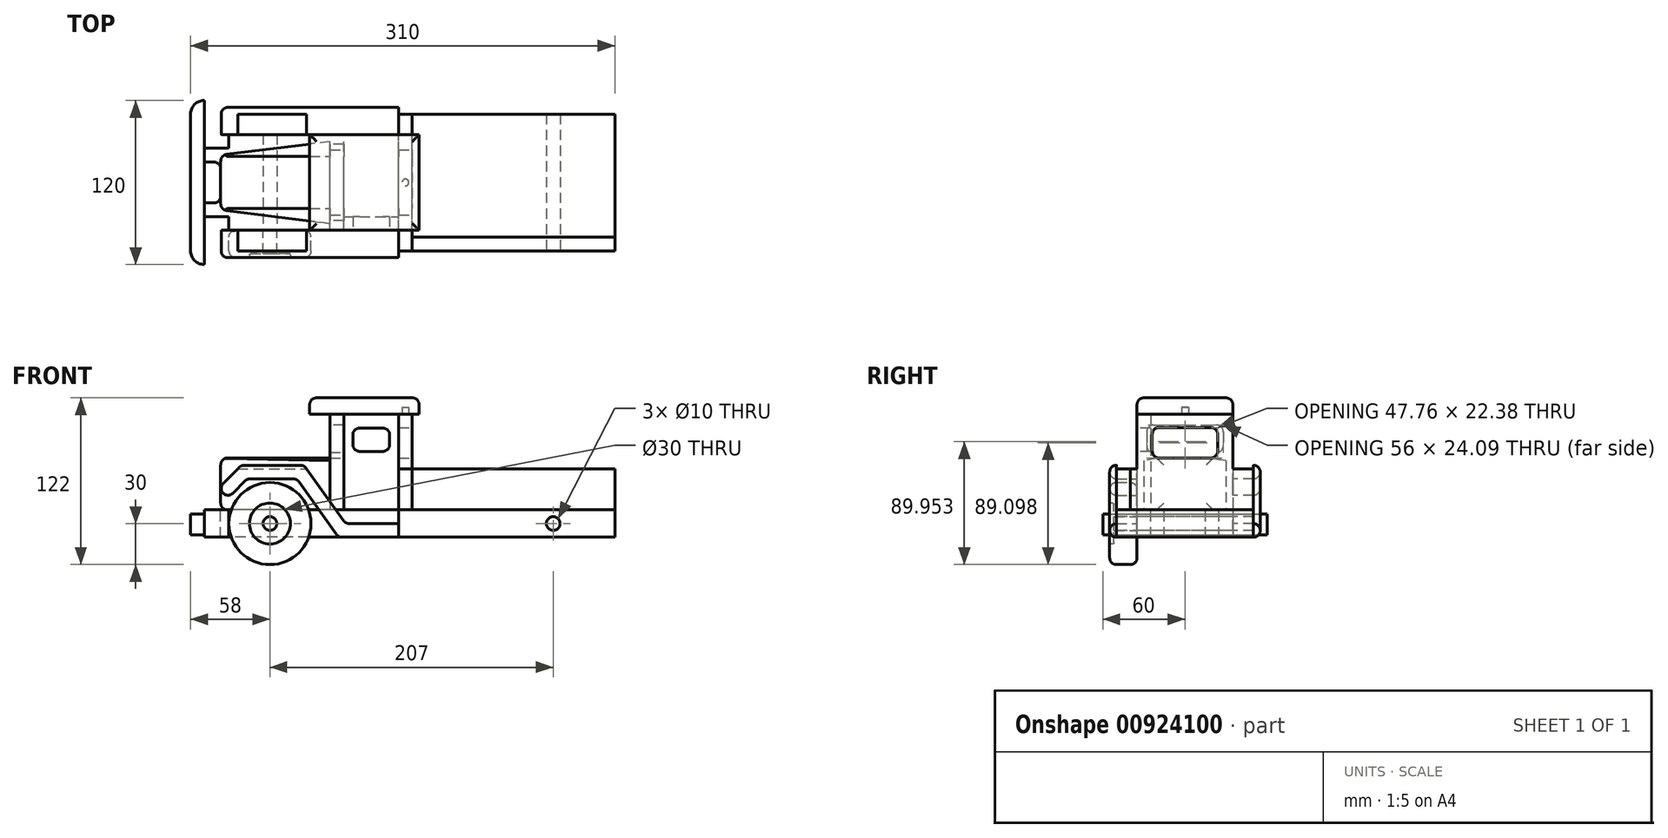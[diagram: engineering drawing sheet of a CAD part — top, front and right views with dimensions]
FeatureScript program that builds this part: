
annotation { "Feature Type Name" : "Feature", "Feature Type Description" : "" }
export const myFeature = defineFeature(function(context is Context, id is Id, definition is map)
    precondition{}
    {
        {
            var Q0;
            Q0=qCreatedBy(makeId("Top.planeOp"),FACE);
            var sketch = newSketch(context, id + "F0", { "sketchPlane" : qUnion([Q0])});
            skLineSegment(sketch, "E0.bottom", {"start": v(-8, 35) * mm, "end": v(-150, 35) * mm});
            skLineSegment(sketch, "E0.top", {"start": v(-8, -35) * mm, "end": v(-150, -35) * mm});
            skLineSegment(sketch, "E0.left", {"start": v(150, 50) * mm, "end": v(150, -50) * mm});
            skLineSegment(sketch, "E0.right", {"start": v(-150, 35) * mm, "end": v(-150, -35) * mm});
            skPoint(sketch, "E0.middle", {"position": v(0, 0) * mm});
            skLineSegment(sketch, "E1", {"start": v(-8, 35) * mm, "end": v(-8, 50) * mm});
            skLineSegment(sketch, "E2", {"start": v(-8, 50) * mm, "end": v(150, 50) * mm});
            skPoint(sketch, "E3.orphan", {"position": v(150, 35) * mm});
            skLineSegment(sketch, "E4", {"start": v(0, 0) * mm, "end": v(192.87, 0) * mm, "construction": true});
            skLineSegment(sketch, "E5.MirrorCS", {"start": v(-8, -50) * mm, "end": v(150, -50) * mm});
            skLineSegment(sketch, "E6.MirrorCS", {"start": v(-8, -35) * mm, "end": v(-8, -50) * mm});
            skPoint(sketch, "E7.MirrorP", {"position": v(150, -35) * mm});
            skSolve(sketch);
        }
        {
            var Q0;
            Q0 = qSketchRegion(id + "F0", true);
            extrude(context, id + "F1", {"entities" : qUnion([Q0]), "depth" : 20 * mm, "offsetDistance" : 25 * mm});
        }
        {
            var Q0;
            Q0=makeQuery(id+"F1.opExtrude","CAP_FACE",FACE,{"disambiguationData":[OSD([sQuery(id+"F0.wireOp",EDGE,"E0.bottom"),sQuery(id+"F0.wireOp",EDGE,"E0.top"),sQuery(id+"F0.wireOp",EDGE,"E0.left"),sQuery(id+"F0.wireOp",EDGE,"E0.right")])],"isStart":false});
            var sketch = newSketch(context, id + "F2", { "sketchPlane" : qUnion([Q0])});
            skLineSegment(sketch, "E8.bottom", {"start": v(-150, 35) * mm, "end": v(-132, 35) * mm});
            skLineSegment(sketch, "E8.top", {"start": v(-150, 25) * mm, "end": v(-132, 25) * mm});
            skLineSegment(sketch, "E8.left", {"start": v(-150, 35) * mm, "end": v(-150, 25) * mm});
            skLineSegment(sketch, "E8.right", {"start": v(-132, 35) * mm, "end": v(-132, 25) * mm});
            skLineSegment(sketch, "E9.bottom", {"start": v(-150, -35) * mm, "end": v(-132, -35) * mm});
            skLineSegment(sketch, "E9.top", {"start": v(-150, -25) * mm, "end": v(-132, -25) * mm});
            skLineSegment(sketch, "E9.left", {"start": v(-150, -35) * mm, "end": v(-150, -25) * mm});
            skLineSegment(sketch, "E9.right", {"start": v(-132, -35) * mm, "end": v(-132, -25) * mm});
            skSolve(sketch);
        }
        {
            var Q0;
            Q0 = qSketchRegion(id + "F2", true);
            extrude(context, id + "F3", {"entities" : qUnion([Q0]), "operationType" : NewBodyOperationType.REMOVE, "endBound" : BoundingType.THROUGH_ALL, "oppositeDirection" : true, "depth" : 25 * mm, "offsetDistance" : 25 * mm});
        }
        {
            var Q0;
            Q0=makeQuery(id+"F1.opExtrude","CAP_FACE",FACE,{"disambiguationData":[OSD([sQuery(id+"F0.wireOp",EDGE,"E0.bottom"),sQuery(id+"F0.wireOp",EDGE,"E0.top"),sQuery(id+"F0.wireOp",EDGE,"E0.left"),sQuery(id+"F0.wireOp",EDGE,"E0.right")])],"isStart":false});
            var sketch = newSketch(context, id + "F4", { "sketchPlane" : qUnion([Q0])});
            skLineSegment(sketch, "E10.bottom", {"start": v(-150, 15) * mm, "end": v(-143, 15) * mm});
            skLineSegment(sketch, "E10.top", {"start": v(-150, -15) * mm, "end": v(-143, -15) * mm});
            skLineSegment(sketch, "E10.left", {"start": v(-150, 15) * mm, "end": v(-150, -15) * mm});
            skLineSegment(sketch, "E10.right", {"start": v(-138, 10) * mm, "end": v(-138, -10) * mm});
            skPoint(sketch, "E11.visualSharp", {"position": v(-138, 15) * mm});
            skArc(sketch, "E11.filletArc", {"start": v(-138, 10) * mm, "mid": v(-139.46, 13.54) * mm, "end": v(-143, 15) * mm});
            skPoint(sketch, "E12.visualSharp", {"position": v(-138, -15) * mm});
            skArc(sketch, "E12.filletArc", {"start": v(-143, -15) * mm, "mid": v(-139.46, -13.54) * mm, "end": v(-138, -10) * mm});
            skSolve(sketch);
        }
        {
            var Q0;
            Q0 = qSketchRegion(id + "F4", true);
            extrude(context, id + "F5", {"entities" : qUnion([Q0]), "operationType" : NewBodyOperationType.REMOVE, "endBound" : BoundingType.THROUGH_ALL, "oppositeDirection" : true, "depth" : 25 * mm, "offsetDistance" : 25 * mm});
        }
        {
            var Q0;
            Q0=makeQuery(id+"F1.opExtrude","CAP_FACE",FACE,{"disambiguationData":[OSD([sQuery(id+"F0.wireOp",EDGE,"E0.bottom"),sQuery(id+"F0.wireOp",EDGE,"E0.top"),sQuery(id+"F0.wireOp",EDGE,"E0.left"),sQuery(id+"F0.wireOp",EDGE,"E0.right")])],"isStart":false});
            var sketch = newSketch(context, id + "F6", { "sketchPlane" : qUnion([Q0])});
            skLineSegment(sketch, "E13.bottom", {"start": v(-58, -35) * mm, "end": v(-48, -35) * mm});
            skLineSegment(sketch, "E13.top", {"start": v(-58, 35) * mm, "end": v(-48, 35) * mm});
            skLineSegment(sketch, "E13.left", {"start": v(-58, -35) * mm, "end": v(-58, 35) * mm});
            skLineSegment(sketch, "E13.right", {"start": v(-48, -35) * mm, "end": v(-48, 35) * mm});
            skSolve(sketch);
        }
        {
            var Q0;
            Q0 = qSketchRegion(id + "F6", true);
            extrude(context, id + "F7", {"entities" : qUnion([Q0]), "depth" : 70 * mm, "offsetDistance" : 25 * mm});
        }
        {
            var Q0;
            Q0=makeQuery(id+"F7.opExtrude","SWEPT_FACE",FACE,{"disambiguationData":[OSD([sQuery(id+"F6.wireOp",EDGE,"E13.left")])]});
            var sketch = newSketch(context, id + "F8", { "sketchPlane" : qUnion([Q0])});
            skLineSegment(sketch, "E14", {"start": v(0, 61.29) * mm, "end": v(30, 56) * mm});
            skLineSegment(sketch, "E15", {"start": v(30, 56) * mm, "end": v(30, 20) * mm});
            skLineSegment(sketch, "E16", {"start": v(30, 20) * mm, "end": v(0, 20) * mm});
            skLineSegment(sketch, "E17", {"start": v(0, 20) * mm, "end": v(0, 68.79) * mm, "construction": true});
            skLineSegment(sketch, "E18.MirrorCS", {"start": v(0, 61.29) * mm, "end": v(-30, 56) * mm});
            skLineSegment(sketch, "E19.MirrorCS", {"start": v(-30, 56) * mm, "end": v(-30, 20) * mm});
            skLineSegment(sketch, "E20.MirrorCS", {"start": v(-30, 20) * mm, "end": v(0, 20) * mm});
            skSolve(sketch);
        }
        {
            var Q0;
            Q0 = qSketchRegion(id + "F8", true);
            extrude(context, id + "F9", {"entities" : qUnion([Q0]), "depth" : 80 * mm, "offsetDistance" : 25 * mm});
        }
        {
            var Q0;
            Q0=makeQuery(id+"F9.opExtrude","SWEPT_FACE",FACE,{"disambiguationData":[OSD([sQuery(id+"F8.wireOp",EDGE,"E16"),sQuery(id+"F8.wireOp",EDGE,"E20.MirrorCS")])]});
            var sketch = newSketch(context, id + "F10", { "sketchPlane" : qUnion([Q0])});
            skLineSegment(sketch, "E21", {"start": v(-58, 30) * mm, "end": v(-138, 20) * mm});
            skLineSegment(sketch, "E22.0", {"start": v(-138, 30) * mm, "end": v(-138, 20) * mm});
            skLineSegment(sketch, "E22.1", {"start": v(-138, 30) * mm, "end": v(-58, 30) * mm});
            skPoint(sketch, "E23.orphan", {"position": v(-138, -30) * mm});
            skLineSegment(sketch, "E24", {"start": v(-58, 0) * mm, "end": v(-100.02, 0) * mm, "construction": true});
            skLineSegment(sketch, "E25.MirrorCS", {"start": v(-58, -30) * mm, "end": v(-138, -20) * mm});
            skLineSegment(sketch, "E26.MirrorCS", {"start": v(-138, -30) * mm, "end": v(-138, -20) * mm});
            skLineSegment(sketch, "E27.MirrorCS", {"start": v(-138, -30) * mm, "end": v(-58, -30) * mm});
            skPoint(sketch, "E28.MirrorP", {"position": v(-138, 30) * mm});
            skSolve(sketch);
        }
        {
            var Q0;
            Q0 = qSketchRegion(id + "F10", true);
            extrude(context, id + "F11", {"entities" : qUnion([Q0]), "operationType" : NewBodyOperationType.REMOVE, "endBound" : BoundingType.THROUGH_ALL, "oppositeDirection" : true, "depth" : 25 * mm, "offsetDistance" : 25 * mm});
        }
        {
            var Q0;
            Q0=makeQuery(id+"F7.opExtrude","SWEPT_FACE",FACE,{"disambiguationData":[OSD([sQuery(id+"F6.wireOp",EDGE,"E13.left")])]});
            var sketch = newSketch(context, id + "F12", { "sketchPlane" : qUnion([Q0])});
            skLineSegment(sketch, "E29.bottom", {"start": v(23, 82) * mm, "end": v(-23, 82) * mm});
            skLineSegment(sketch, "E29.top", {"start": v(23, 62) * mm, "end": v(-23, 62) * mm});
            skLineSegment(sketch, "E29.left", {"start": v(28, 77) * mm, "end": v(28, 67) * mm});
            skLineSegment(sketch, "E29.right", {"start": v(-28, 77) * mm, "end": v(-28, 67) * mm});
            skPoint(sketch, "E29.middle", {"position": v(0, 72) * mm});
            skPoint(sketch, "E29.middle.positionSnap0", {"position": v(0, 90) * mm});
            skPoint(sketch, "E29.centerSnap0", {"position": v(0, 90) * mm});
            skPoint(sketch, "E30.visualSharp", {"position": v(-28, 82) * mm});
            skArc(sketch, "E30.filletArc", {"start": v(-23, 82) * mm, "mid": v(-26.54, 80.54) * mm, "end": v(-28, 77) * mm});
            skPoint(sketch, "E31.visualSharp", {"position": v(-28, 62) * mm});
            skArc(sketch, "E31.filletArc", {"start": v(-28, 67) * mm, "mid": v(-26.54, 63.46) * mm, "end": v(-23, 62) * mm});
            skPoint(sketch, "E32.visualSharp", {"position": v(28, 62) * mm});
            skArc(sketch, "E32.filletArc", {"start": v(23, 62) * mm, "mid": v(26.54, 63.46) * mm, "end": v(28, 67) * mm});
            skPoint(sketch, "E33.visualSharp", {"position": v(28, 82) * mm});
            skArc(sketch, "E33.filletArc", {"start": v(28, 77) * mm, "mid": v(26.54, 80.54) * mm, "end": v(23, 82) * mm});
            skSolve(sketch);
        }
        {
            var Q0;
            Q0 = qSketchRegion(id + "F12", true);
            extrude(context, id + "F13", {"entities" : qUnion([Q0]), "operationType" : NewBodyOperationType.REMOVE, "endBound" : BoundingType.THROUGH_ALL, "oppositeDirection" : true, "depth" : 25 * mm, "offsetDistance" : 25 * mm});
        }
        {
            var Q0;
            Q0=makeQuery(id+"F1.opExtrude","CAP_FACE",FACE,{"disambiguationData":[OSD([sQuery(id+"F0.wireOp",EDGE,"E0.bottom"),sQuery(id+"F0.wireOp",EDGE,"E0.top"),sQuery(id+"F0.wireOp",EDGE,"E0.left"),sQuery(id+"F0.wireOp",EDGE,"E0.right")])],"isStart":false});
            var sketch = newSketch(context, id + "F14", { "sketchPlane" : qUnion([Q0])});
            skLineSegment(sketch, "E34.bottom", {"start": v(-48, -35) * mm, "end": v(-8, -35) * mm});
            skLineSegment(sketch, "E34.top", {"start": v(-48, -25) * mm, "end": v(-8, -25) * mm});
            skLineSegment(sketch, "E34.left", {"start": v(-48, -35) * mm, "end": v(-48, -25) * mm});
            skLineSegment(sketch, "E34.right", {"start": v(-8, -35) * mm, "end": v(-8, -25) * mm});
            skSolve(sketch);
        }
        {
            var Q0;
            Q0 = qSketchRegion(id + "F14", true);
            extrude(context, id + "F15", {"entities" : qUnion([Q0]), "depth" : 70 * mm, "offsetDistance" : 25 * mm});
        }
        {
            var Q0;
            Q0=makeQuery(id+"F1.opExtrude","CAP_FACE",FACE,{"disambiguationData":[OSD([sQuery(id+"F0.wireOp",EDGE,"E0.bottom"),sQuery(id+"F0.wireOp",EDGE,"E0.top"),sQuery(id+"F0.wireOp",EDGE,"E0.left"),sQuery(id+"F0.wireOp",EDGE,"E0.right")])],"isStart":false});
            var sketch = newSketch(context, id + "F16", { "sketchPlane" : qUnion([Q0])});
            skLineSegment(sketch, "E35.bottom", {"start": v(-8, -50) * mm, "end": v(2, -50) * mm});
            skLineSegment(sketch, "E35.top", {"start": v(-8, 50) * mm, "end": v(2, 50) * mm});
            skLineSegment(sketch, "E35.left", {"start": v(-8, -50) * mm, "end": v(-8, 50) * mm});
            skLineSegment(sketch, "E35.right", {"start": v(2, -50) * mm, "end": v(2, 50) * mm});
            skSolve(sketch);
        }
        {
            var Q0;
            Q0 = qSketchRegion(id + "F16", true);
            extrude(context, id + "F17", {"entities" : qUnion([Q0]), "depth" : 70 * mm, "offsetDistance" : 25 * mm});
        }
        {
            var Q0;
            Q0=makeQuery(id+"F17.opExtrude","CAP_FACE",FACE,{"disambiguationData":[OSD([sQuery(id+"F16.wireOp",EDGE,"E35.bottom"),sQuery(id+"F16.wireOp",EDGE,"E35.top"),sQuery(id+"F16.wireOp",EDGE,"E35.left"),sQuery(id+"F16.wireOp",EDGE,"E35.right")])],"isStart":false});
            var sketch = newSketch(context, id + "F18", { "sketchPlane" : qUnion([Q0])});
            skLineSegment(sketch, "E36.bottom", {"start": v(7, 35) * mm, "end": v(-73, 35) * mm});
            skLineSegment(sketch, "E36.top", {"start": v(7, -35) * mm, "end": v(-73, -35) * mm});
            skLineSegment(sketch, "E36.left", {"start": v(7, 35) * mm, "end": v(7, -35) * mm});
            skLineSegment(sketch, "E36.right", {"start": v(-73, 35) * mm, "end": v(-73, -35) * mm});
            skPoint(sketch, "E36.middle", {"position": v(-174.54, 0) * mm});
            skPoint(sketch, "E36.middle.positionSnap0", {"position": v(2, 0) * mm});
            skPoint(sketch, "E36.centerSnap0", {"position": v(2, 0) * mm});
            skSolve(sketch);
        }
        {
            var Q0;
            Q0 = qSketchRegion(id + "F18", true);
            extrude(context, id + "F19", {"entities" : qUnion([Q0]), "depth" : 12 * mm, "offsetDistance" : 25 * mm});
        }
        {
            var Q0;
            Q0=makeQuery(id+"F1.opExtrude","CAP_FACE",FACE,{"disambiguationData":[OSD([sQuery(id+"F0.wireOp",EDGE,"E0.bottom"),sQuery(id+"F0.wireOp",EDGE,"E0.top"),sQuery(id+"F0.wireOp",EDGE,"E0.left"),sQuery(id+"F0.wireOp",EDGE,"E0.right")])],"isStart":false});
            var sketch = newSketch(context, id + "F20", { "sketchPlane" : qUnion([Q0])});
            skLineSegment(sketch, "E37.bottom", {"start": v(2, -50) * mm, "end": v(150, -50) * mm});
            skLineSegment(sketch, "E37.top", {"start": v(2, -40) * mm, "end": v(150, -40) * mm});
            skLineSegment(sketch, "E37.left", {"start": v(2, -50) * mm, "end": v(2, -40) * mm});
            skLineSegment(sketch, "E37.right", {"start": v(150, -50) * mm, "end": v(150, -40) * mm});
            skSolve(sketch);
        }
        {
            var Q0;
            Q0 = qSketchRegion(id + "F20", true);
            extrude(context, id + "F21", {"entities" : qUnion([Q0]), "depth" : 30 * mm, "offsetDistance" : 25 * mm});
        }
        {
            var Q0;
            Q0=makeQuery(id+"F1.opExtrude","SWEPT_FACE",FACE,{"disambiguationData":[OSD([sQuery(id+"F0.wireOp",EDGE,"E0.top")])]});
            var sketch = newSketch(context, id + "F22", { "sketchPlane" : qUnion([Q0])});
            skCircle(sketch, "E38", {"center": v(-102, 10) * mm, "radius": 5 * mm});
            skPoint(sketch, "E38.centerSnap0", {"position": v(-132, 10) * mm});
            skCircle(sketch, "E39", {"center": v(105, 10) * mm, "radius": 5 * mm});
            skPoint(sketch, "E39.centerSnap0", {"position": v(150, 10) * mm});
            skSolve(sketch);
        }
        {
            var Q0;
            Q0 = qSketchRegion(id + "F22", true);
            extrude(context, id + "F23", {"entities" : qUnion([Q0]), "operationType" : NewBodyOperationType.REMOVE, "endBound" : BoundingType.THROUGH_ALL, "oppositeDirection" : true, "depth" : 25 * mm, "offsetDistance" : 25 * mm, "hasSecondDirection" : true, "secondDirectionBound" : SecondDirectionBoundingType.THROUGH_ALL, "secondDirectionOppositeDirection" : false, "secondDirectionDepth" : 25 * mm});
        }
        {
            var Q0;
            Q0=makeQuery(id+"F1.opExtrude","SWEPT_FACE",FACE,{"disambiguationData":[OSD([sQuery(id+"F0.wireOp",EDGE,"E0.top")])]});
            var sketch = newSketch(context, id + "F24", { "sketchPlane" : qUnion([Q0])});
            skCircle(sketch, "E40", {"center": v(-102, 10) * mm, "radius": 30 * mm});
            skCircle(sketch, "E41", {"center": v(-102, 10) * mm, "radius": 5 * mm});
            skSolve(sketch);
        }
        {
            var Q0;
            Q0 = qSketchRegion(id + "F24", true);
            extrude(context, id + "F25", {"entities" : qUnion([Q0]), "depth" : 20 * mm, "offsetDistance" : 25 * mm});
        }
        {
            var Q0;
            Q0=makeQuery(id+"F25.opExtrude","CAP_EDGE",EDGE,{"disambiguationData":[OSD([sQuery(id+"F24.wireOp",EDGE,"E40")])],"isStart":false});
            var Q1;
            Q1=makeQuery(id+"F25.opExtrude","CAP_EDGE",EDGE,{"disambiguationData":[OSD([sQuery(id+"F24.wireOp",EDGE,"E40")])],"isStart":true});
            fillet(context, id + "F26", {"entities" : qUnion([Q0, Q1]), "radius" : 5 * mm, "tangentPropagation" : true, "allowEdgeOverflow" : false});
        }
        {
            var Q0;
            Q0=makeQuery(id+"F25.opExtrude","CAP_FACE",FACE,{"disambiguationData":[OSD([sQuery(id+"F24.wireOp",EDGE,"E40"),sQuery(id+"F24.wireOp",EDGE,"E41")])],"isStart":false});
            var sketch = newSketch(context, id + "F27", { "sketchPlane" : qUnion([Q0])});
            skCircle(sketch, "E42", {"center": v(-102, 10) * mm, "radius": 15 * mm});
            skSolve(sketch);
        }
        {
            var Q0;
            Q0 = qSketchRegion(id + "F27", true);
            extrude(context, id + "F28", {"entities" : qUnion([Q0]), "operationType" : NewBodyOperationType.REMOVE, "oppositeDirection" : true, "depth" : 3 * mm, "offsetDistance" : 25 * mm});
        }
        {
            var Q0;
            Q0=makeQuery(id+"F28.boolean.opBoolean","COPY",EDGE,{"derivedFrom":makeQuery(id+"F28.opExtrude","CAP_EDGE",EDGE,{"disambiguationData":[OSD([sQuery(id+"F27.wireOp",EDGE,"E42")])],"isStart":false})});
            var Q1;
            Q1=makeQuery(id+"F28.boolean.opBoolean","COPY",EDGE,{"derivedFrom":makeQuery(id+"F28.opExtrude","CAP_EDGE",EDGE,{"disambiguationData":[OSD([sQuery(id+"F27.wireOp",EDGE,"E42")])],"isStart":true})});
            fillet(context, id + "F29", {"entities" : qUnion([Q0, Q1]), "radius" : 1 * mm, "tangentPropagation" : true, "allowEdgeOverflow" : false});
        }
        {
            var Q0;
            Q0=makeQuery(id+"F19.opExtrude","CAP_FACE",FACE,{"disambiguationData":[OSD([sQuery(id+"F18.wireOp",EDGE,"E36.bottom"),sQuery(id+"F18.wireOp",EDGE,"E36.top"),sQuery(id+"F18.wireOp",EDGE,"E36.left"),sQuery(id+"F18.wireOp",EDGE,"E36.right")])],"isStart":false});
            fillet(context, id + "F30", {"entities" : qUnion([Q0]), "radius" : 5 * mm, "tangentPropagation" : true, "allowEdgeOverflow" : false});
        }
        {
            var Q0;
            Q0=makeQuery(id+"F15.opExtrude","SWEPT_FACE",FACE,{"disambiguationData":[OSD([sQuery(id+"F14.wireOp",EDGE,"E34.bottom")])]});
            var sketch = newSketch(context, id + "F31", { "sketchPlane" : qUnion([Q0])});
            skLineSegment(sketch, "E43.bottom", {"start": v(-19.57, 79.88) * mm, "end": v(-36.43, 79.88) * mm});
            skLineSegment(sketch, "E43.top", {"start": v(-19.57, 62.78) * mm, "end": v(-36.43, 62.78) * mm});
            skLineSegment(sketch, "E43.left", {"start": v(-14.57, 74.88) * mm, "end": v(-14.57, 67.78) * mm});
            skLineSegment(sketch, "E43.right", {"start": v(-41.43, 74.88) * mm, "end": v(-41.43, 67.78) * mm});
            skPoint(sketch, "E43.middle", {"position": v(-28, 71.33) * mm});
            skPoint(sketch, "E43.middle.positionSnap0", {"position": v(-28, 90) * mm});
            skPoint(sketch, "E43.centerSnap0", {"position": v(-28, 90) * mm});
            skPoint(sketch, "E44.visualSharp", {"position": v(-41.43, 79.88) * mm});
            skArc(sketch, "E44.filletArc", {"start": v(-36.43, 79.88) * mm, "mid": v(-39.97, 78.42) * mm, "end": v(-41.43, 74.88) * mm});
            skPoint(sketch, "E45.visualSharp", {"position": v(-41.43, 62.78) * mm});
            skArc(sketch, "E45.filletArc", {"start": v(-41.43, 67.78) * mm, "mid": v(-39.97, 64.25) * mm, "end": v(-36.43, 62.78) * mm});
            skPoint(sketch, "E46.visualSharp", {"position": v(-14.57, 62.78) * mm});
            skArc(sketch, "E46.filletArc", {"start": v(-19.57, 62.78) * mm, "mid": v(-16.03, 64.25) * mm, "end": v(-14.57, 67.78) * mm});
            skPoint(sketch, "E47.visualSharp", {"position": v(-14.57, 79.88) * mm});
            skArc(sketch, "E47.filletArc", {"start": v(-14.57, 74.88) * mm, "mid": v(-16.03, 78.42) * mm, "end": v(-19.57, 79.88) * mm});
            skSolve(sketch);
        }
        {
            var Q0;
            Q0 = qSketchRegion(id + "F31", true);
            extrude(context, id + "F32", {"entities" : qUnion([Q0]), "operationType" : NewBodyOperationType.REMOVE, "endBound" : BoundingType.THROUGH_ALL, "oppositeDirection" : true, "depth" : 25 * mm, "offsetDistance" : 25 * mm});
        }
        {
            var Q0;
            Q0=makeQuery(id+"F19.opExtrude","CAP_FACE",FACE,{"disambiguationData":[OSD([sQuery(id+"F18.wireOp",EDGE,"E36.bottom"),sQuery(id+"F18.wireOp",EDGE,"E36.top"),sQuery(id+"F18.wireOp",EDGE,"E36.left"),sQuery(id+"F18.wireOp",EDGE,"E36.right")])],"isStart":true});
            var sketch = newSketch(context, id + "F33", { "sketchPlane" : qUnion([Q0])});
            skCircle(sketch, "E48", {"center": v(-3, 0) * mm, "radius": 2.47 * mm});
            skPoint(sketch, "E49", {"position": v(7, 0) * mm});
            skSolve(sketch);
        }
        {
            var Q0;
            Q0 = qSketchRegion(id + "F33", true);
            extrude(context, id + "F34", {"entities" : qUnion([Q0]), "operationType" : NewBodyOperationType.REMOVE, "oppositeDirection" : true, "depth" : 5 * mm, "offsetDistance" : 25 * mm});
        }
        {
            var Q0;
            Q0=makeQuery(id+"F17.opExtrude","SWEPT_FACE",FACE,{"disambiguationData":[OSD([sQuery(id+"F16.wireOp",EDGE,"E35.right")])]});
            var sketch = newSketch(context, id + "F35", { "sketchPlane" : qUnion([Q0])});
            skLineSegment(sketch, "E50.bottom", {"start": v(18.88, 80.29) * mm, "end": v(-18.88, 80.29) * mm});
            skLineSegment(sketch, "E50.top", {"start": v(18.88, 57.9) * mm, "end": v(-18.88, 57.9) * mm});
            skLineSegment(sketch, "E50.left", {"start": v(23.88, 75.29) * mm, "end": v(23.88, 62.9) * mm});
            skLineSegment(sketch, "E50.right", {"start": v(-23.88, 75.29) * mm, "end": v(-23.88, 62.9) * mm});
            skPoint(sketch, "E50.middle", {"position": v(0, 69.1) * mm});
            skPoint(sketch, "E51.visualSharp", {"position": v(-23.88, 80.29) * mm});
            skArc(sketch, "E51.filletArc", {"start": v(-18.88, 80.29) * mm, "mid": v(-22.42, 78.82) * mm, "end": v(-23.88, 75.29) * mm});
            skPoint(sketch, "E52.visualSharp", {"position": v(-23.88, 57.9) * mm});
            skArc(sketch, "E52.filletArc", {"start": v(-23.88, 62.9) * mm, "mid": v(-22.42, 59.37) * mm, "end": v(-18.88, 57.9) * mm});
            skPoint(sketch, "E53.visualSharp", {"position": v(23.88, 57.9) * mm});
            skArc(sketch, "E53.filletArc", {"start": v(18.88, 57.9) * mm, "mid": v(22.42, 59.37) * mm, "end": v(23.88, 62.9) * mm});
            skPoint(sketch, "E54.visualSharp", {"position": v(23.88, 80.29) * mm});
            skArc(sketch, "E54.filletArc", {"start": v(23.88, 75.29) * mm, "mid": v(22.42, 78.82) * mm, "end": v(18.88, 80.29) * mm});
            skSolve(sketch);
        }
        {
            var Q0;
            Q0 = qSketchRegion(id + "F35", true);
            extrude(context, id + "F36", {"entities" : qUnion([Q0]), "operationType" : NewBodyOperationType.REMOVE, "endBound" : BoundingType.THROUGH_ALL, "oppositeDirection" : true, "depth" : 25 * mm, "offsetDistance" : 25 * mm});
        }
        {
            var Q0;
            {var subQ4=sQuery(id+"F0.wireOp",EDGE,"E0.right");Q0=makeQuery(id+"F5.boolean.opBoolean","SPLIT",FACE,{"disambiguationData":[TD([makeQuery(id+"F3.boolean.opBoolean","COPY",FACE,{"derivedFrom":makeQuery(id+"F3.opExtrude","SWEPT_FACE",FACE,{"disambiguationData":[OSD([sQuery(id+"F2.wireOp",EDGE,"E8.top")])]})})])],"derivedFrom":makeQuery(id+"F1.opExtrude","SWEPT_FACE",FACE,{"disambiguationData":[OSD([subQ4])]})});}
            var sketch = newSketch(context, id + "F37", { "sketchPlane" : qUnion([Q0])});
            skLineSegment(sketch, "E55.bottom", {"start": v(60, 17.03) * mm, "end": v(-60, 17.03) * mm});
            skLineSegment(sketch, "E55.top", {"start": v(60, 1.66) * mm, "end": v(-60, 1.66) * mm});
            skLineSegment(sketch, "E55.left", {"start": v(60, 17.03) * mm, "end": v(60, 1.66) * mm});
            skLineSegment(sketch, "E55.right", {"start": v(-60, 17.03) * mm, "end": v(-60, 1.66) * mm});
            skPoint(sketch, "E55.middle", {"position": v(0, 9.35) * mm});
            skSolve(sketch);
        }
        {
            var Q0;
            Q0 = qSketchRegion(id + "F37", true);
            extrude(context, id + "F38", {"entities" : qUnion([Q0]), "depth" : 10 * mm, "offsetDistance" : 25 * mm});
        }
        {
            var Q0;
            Q0=makeQuery(id+"F38.opExtrude","CAP_EDGE",EDGE,{"disambiguationData":[OSD([sQuery(id+"F37.wireOp",EDGE,"E55.right")])],"isStart":false});
            var Q1;
            Q1=makeQuery(id+"F38.opExtrude","CAP_EDGE",EDGE,{"disambiguationData":[OSD([sQuery(id+"F37.wireOp",EDGE,"E55.left")])],"isStart":false});
            fillet(context, id + "F39", {"entities" : qUnion([Q0, Q1]), "radius" : 10 * mm, "tangentPropagation" : true, "allowEdgeOverflow" : false});
        }
        {
            var Q0;
            Q0=makeQuery(id+"F9.opExtrude","CAP_FACE",FACE,{"disambiguationData":[OSD([sQuery(id+"F8.wireOp",EDGE,"E14"),sQuery(id+"F8.wireOp",EDGE,"E15"),sQuery(id+"F8.wireOp",EDGE,"E16"),sQuery(id+"F8.wireOp",EDGE,"E18.MirrorCS"),sQuery(id+"F8.wireOp",EDGE,"E19.MirrorCS"),sQuery(id+"F8.wireOp",EDGE,"E20.MirrorCS")])],"isStart":false});
            fillet(context, id + "F40", {"entities" : qUnion([Q0]), "radius" : 5 * mm, "tangentPropagation" : true, "allowEdgeOverflow" : false});
        }
        {
            var Q0;
            Q0=makeQuery(id+"F1.opExtrude","SWEPT_FACE",FACE,{"disambiguationData":[OSD([sQuery(id+"F0.wireOp",EDGE,"E0.top")])]});
            var sketch = newSketch(context, id + "F41", { "sketchPlane" : qUnion([Q0])});
            skLineSegment(sketch, "E56", {"start": v(-129.04, 32.22) * mm, "end": v(-120.27, 41.17) * mm});
            skLineSegment(sketch, "E57", {"start": v(-116.7, 42.66) * mm, "end": v(-84.8, 42.66) * mm});
            skLineSegment(sketch, "E58", {"start": v(-80.73, 40.56) * mm, "end": v(-53.42, 2.1) * mm});
            skLineSegment(sketch, "E59.0", {"start": v(-75.56, 50.56) * mm, "end": v(-48.25, 12.1) * mm});
            skLineSegment(sketch, "E59.1", {"start": v(-120.9, 52.66) * mm, "end": v(-79.64, 52.66) * mm});
            skLineSegment(sketch, "E59.2", {"start": v(-136.18, 39.23) * mm, "end": v(-124.47, 51.17) * mm});
            skLineSegment(sketch, "E60", {"start": v(-136.11, 32.15) * mm, "end": v(-136.11, 32.15) * mm});
            skLineSegment(sketch, "E61.0", {"start": v(-8, 0) * mm, "end": v(-49.34, 0) * mm});
            skLineSegment(sketch, "E62.0", {"start": v(-8, 10) * mm, "end": v(-44.18, 10) * mm});
            skPoint(sketch, "E63.orphan", {"position": v(-132, 0) * mm});
            skLineSegment(sketch, "E64.0", {"start": v(-8, 10) * mm, "end": v(-8, 0) * mm});
            skPoint(sketch, "E65.orphan", {"position": v(-8, 20) * mm});
            skPoint(sketch, "E66.visualSharp", {"position": v(-132.54, 28.65) * mm});
            skArc(sketch, "E66.filletArc", {"start": v(-136.11, 32.15) * mm, "mid": v(-132.56, 30.72) * mm, "end": v(-129.04, 32.22) * mm});
            skPoint(sketch, "E67.visualSharp", {"position": v(-139.68, 35.66) * mm});
            skArc(sketch, "E67.filletArc", {"start": v(-136.18, 39.23) * mm, "mid": v(-137.6, 35.68) * mm, "end": v(-136.11, 32.15) * mm});
            skPoint(sketch, "E68.visualSharp", {"position": v(-123, 52.66) * mm});
            skArc(sketch, "E68.filletArc", {"start": v(-120.9, 52.66) * mm, "mid": v(-122.83, 52.27) * mm, "end": v(-124.47, 51.17) * mm});
            skPoint(sketch, "E69.visualSharp", {"position": v(-118.8, 42.66) * mm});
            skArc(sketch, "E69.filletArc", {"start": v(-116.7, 42.66) * mm, "mid": v(-118.64, 42.27) * mm, "end": v(-120.27, 41.17) * mm});
            skPoint(sketch, "E70.visualSharp", {"position": v(-82.22, 42.66) * mm});
            skArc(sketch, "E70.filletArc", {"start": v(-80.73, 40.56) * mm, "mid": v(-82.5, 42.1) * mm, "end": v(-84.8, 42.66) * mm});
            skPoint(sketch, "E71.visualSharp", {"position": v(-77.06, 52.66) * mm});
            skArc(sketch, "E71.filletArc", {"start": v(-75.56, 50.56) * mm, "mid": v(-77.35, 52.1) * mm, "end": v(-79.64, 52.66) * mm});
            skPoint(sketch, "E72.visualSharp", {"position": v(-46.76, 10) * mm});
            skArc(sketch, "E72.filletArc", {"start": v(-48.25, 12.1) * mm, "mid": v(-46.47, 10.56) * mm, "end": v(-44.18, 10) * mm});
            skPoint(sketch, "E73.visualSharp", {"position": v(-51.92, 0) * mm});
            skArc(sketch, "E73.filletArc", {"start": v(-53.42, 2.1) * mm, "mid": v(-51.63, 0.56) * mm, "end": v(-49.34, 0) * mm});
            skSolve(sketch);
        }
        {
            var Q0;
            Q0 = qSketchRegion(id + "F41", true);
            extrude(context, id + "F42", {"entities" : qUnion([Q0]), "depth" : 20 * mm, "offsetDistance" : 25 * mm});
        }
        {
            var Q0;
            Q0=makeQuery(id+"F42.opExtrude","CAP_EDGE",EDGE,{"disambiguationData":[OSD([sQuery(id+"F41.wireOp",EDGE,"E59.2")])],"isStart":false});
            fillet(context, id + "F43", {"entities" : qUnion([Q0]), "radius" : 5 * mm, "tangentPropagation" : true, "allowEdgeOverflow" : false});
        }
        {
            var Q0;
            Q0=makeQuery(id+"F42.opExtrude","SWEPT_BODY",BODY,{"disambiguationData":[OSD([sQuery(id+"F41.wireOp",EDGE,"E56"),sQuery(id+"F41.wireOp",EDGE,"E57"),sQuery(id+"F41.wireOp",EDGE,"E58"),sQuery(id+"F41.wireOp",EDGE,"E59.0"),sQuery(id+"F41.wireOp",EDGE,"E59.1"),sQuery(id+"F41.wireOp",EDGE,"E59.2"),sQuery(id+"F41.wireOp",EDGE,"E61.0"),sQuery(id+"F41.wireOp",EDGE,"E62.0"),sQuery(id+"F41.wireOp",EDGE,"E64.0"),sQuery(id+"F41.wireOp",EDGE,"E66.filletArc"),sQuery(id+"F41.wireOp",EDGE,"E67.filletArc"),sQuery(id+"F41.wireOp",EDGE,"E68.filletArc"),sQuery(id+"F41.wireOp",EDGE,"E69.filletArc"),sQuery(id+"F41.wireOp",EDGE,"E70.filletArc"),sQuery(id+"F41.wireOp",EDGE,"E71.filletArc"),sQuery(id+"F41.wireOp",EDGE,"E72.filletArc"),sQuery(id+"F41.wireOp",EDGE,"E73.filletArc")])]});
            var Q1;
            Q1=qCreatedBy(makeId("Front.planeOp"),FACE);
            mirror(context, id + "F44", {"entities" : qUnion([Q0]), "mirrorPlane" : qUnion([Q1])});
        }
        {
            var Q0;
            Q0=makeQuery(id+"F17.opExtrude","SWEPT_FACE",FACE,{"disambiguationData":[OSD([sQuery(id+"F16.wireOp",EDGE,"E35.right")])]});
            var sketch = newSketch(context, id + "F45", { "sketchPlane" : qUnion([Q0])});
            skLineSegment(sketch, "E74.bottom", {"start": v(-50, 50) * mm, "end": v(-35, 50) * mm});
            skLineSegment(sketch, "E74.top", {"start": v(-50, 90) * mm, "end": v(-35, 90) * mm});
            skLineSegment(sketch, "E74.left", {"start": v(-50, 50) * mm, "end": v(-50, 90) * mm});
            skLineSegment(sketch, "E74.right", {"start": v(-35, 50) * mm, "end": v(-35, 90) * mm});
            skLineSegment(sketch, "E75.bottom", {"start": v(50, 90) * mm, "end": v(35, 90) * mm});
            skLineSegment(sketch, "E75.top", {"start": v(50, 50) * mm, "end": v(35, 50) * mm});
            skLineSegment(sketch, "E75.left", {"start": v(50, 90) * mm, "end": v(50, 50) * mm});
            skLineSegment(sketch, "E75.right", {"start": v(35, 90) * mm, "end": v(35, 50) * mm});
            skSolve(sketch);
        }
        {
            var Q0;
            Q0 = qSketchRegion(id + "F45", true);
            extrude(context, id + "F46", {"entities" : qUnion([Q0]), "operationType" : NewBodyOperationType.REMOVE, "endBound" : BoundingType.THROUGH_ALL, "oppositeDirection" : true, "depth" : 25 * mm, "offsetDistance" : 25 * mm});
        }
    });
